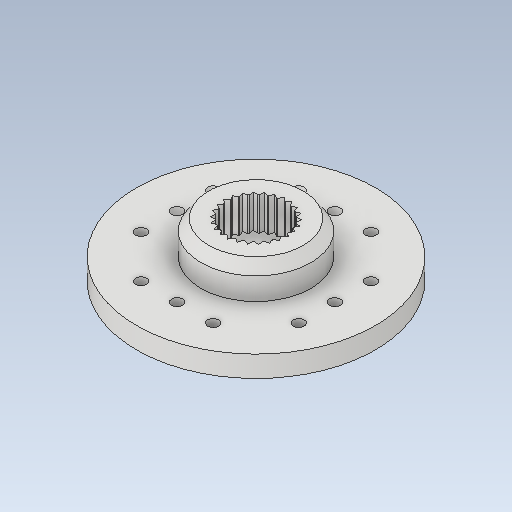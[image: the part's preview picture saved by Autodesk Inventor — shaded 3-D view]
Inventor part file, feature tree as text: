
AUTODESK INVENTOR PART (.ipt)
format: ipt  version: 2021.2 (Build 252289000, 289)  size: 298,496 bytes
history: native  units: mm
features: extrude x7, sketch x7, other x1, chamfer x1, pattern_circular x1
ambient origin geometry x8: Origin, YZ Plane, XZ Plane, XY Plane, X Axis, Y Axis, Z Axis, Center Point
bodies: Body1 (feature_tree)
feature tree (17):
  other  "Sólido1"
  extrude  "Extrusión1"  Depth=1.0mm
  extrude  "Extrusión2"  Depth=7.1mm
  chamfer  "Chaflán1"  Distance=40.0mm Angle=360.0deg
  extrude  "Extrusión4"  Depth=1.9mm
  extrude  "Extrusión5"  Depth=3.0mm
  extrude  "Extrusión7"  Depth=0.5mm
  pattern_circular  "Patrón circular1"  [2 undecoded]
  extrude  "Extrusión8"  Depth=3.0mm
  extrude  "Extrusión9"  Depth=3.0mm
  sketch  "Boceto1"  dims[d0=21.5mm d1=1.0mm]
  sketch  "Boceto2"  dims[d2=6.5mm d4=7.1mm d5=40.0mm d7=360.0deg]
  sketch  "Boceto6"  dims[d9=1.9mm d10=0.0mm d11=9.9mm]
  sketch  "Boceto7"  dims[d12=3.0mm d13=0.0mm d18=0.7mm d19=2.0mm d20=9.599311mm]
  sketch  "Boceto9"  dims[d24=6.5mm d25=0.5mm]
  sketch  "Boceto10"  dims[d26=1.0mm d27=0.0mm]
  sketch  "Boceto11"  dims[d28=8.5mm d29=0.4mm d30=0.0mm d34=5.2mm d37=13.962634mm d38=0.525825mm d39=3.0mm d40=0.0mm d41=260.0mm d42=360.0deg d44=3.0mm d45=0.0mm d46=2.8mm d47=3.0mm d48=0.0mm]
note: 2 required parameter values undecoded (feature->parameter linkage not recoverable at this tier; creation-order binding heuristic only, values carry confidence <= 0.55)
